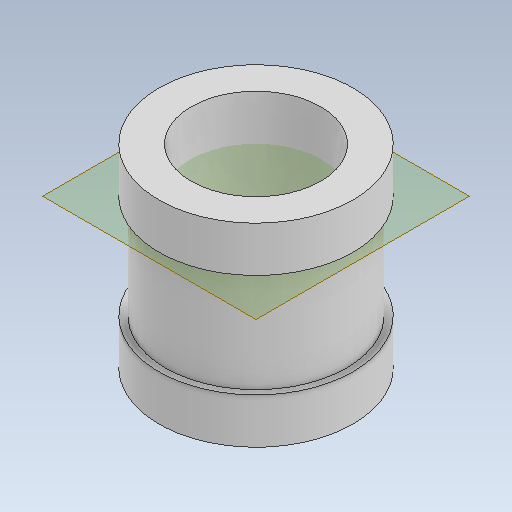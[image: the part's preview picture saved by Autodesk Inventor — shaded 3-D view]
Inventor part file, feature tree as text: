
AUTODESK INVENTOR PART (.ipt)
format: ipt  version: 2020 (Build 240168000, 168)  size: 117,248 bytes
history: native  units: mm
features: other x3, sketch x2, plane x1
ambient origin geometry x8: Origin, YZ Plane, XZ Plane, XY Plane, X Axis, Y Axis, Z Axis, Center Point
bodies: Solid1 (feature_tree)
feature tree (6):
  other  "screw_holder_2_3.ipt"
  other  "Solid1::screw_holder_2_3.ipt"
  other  "TaggingFeature1"
  sketch  "Sketch1"  dims[d0=10.0mm]
  sketch  "Sketch2"
  plane  "Work Plane1"
